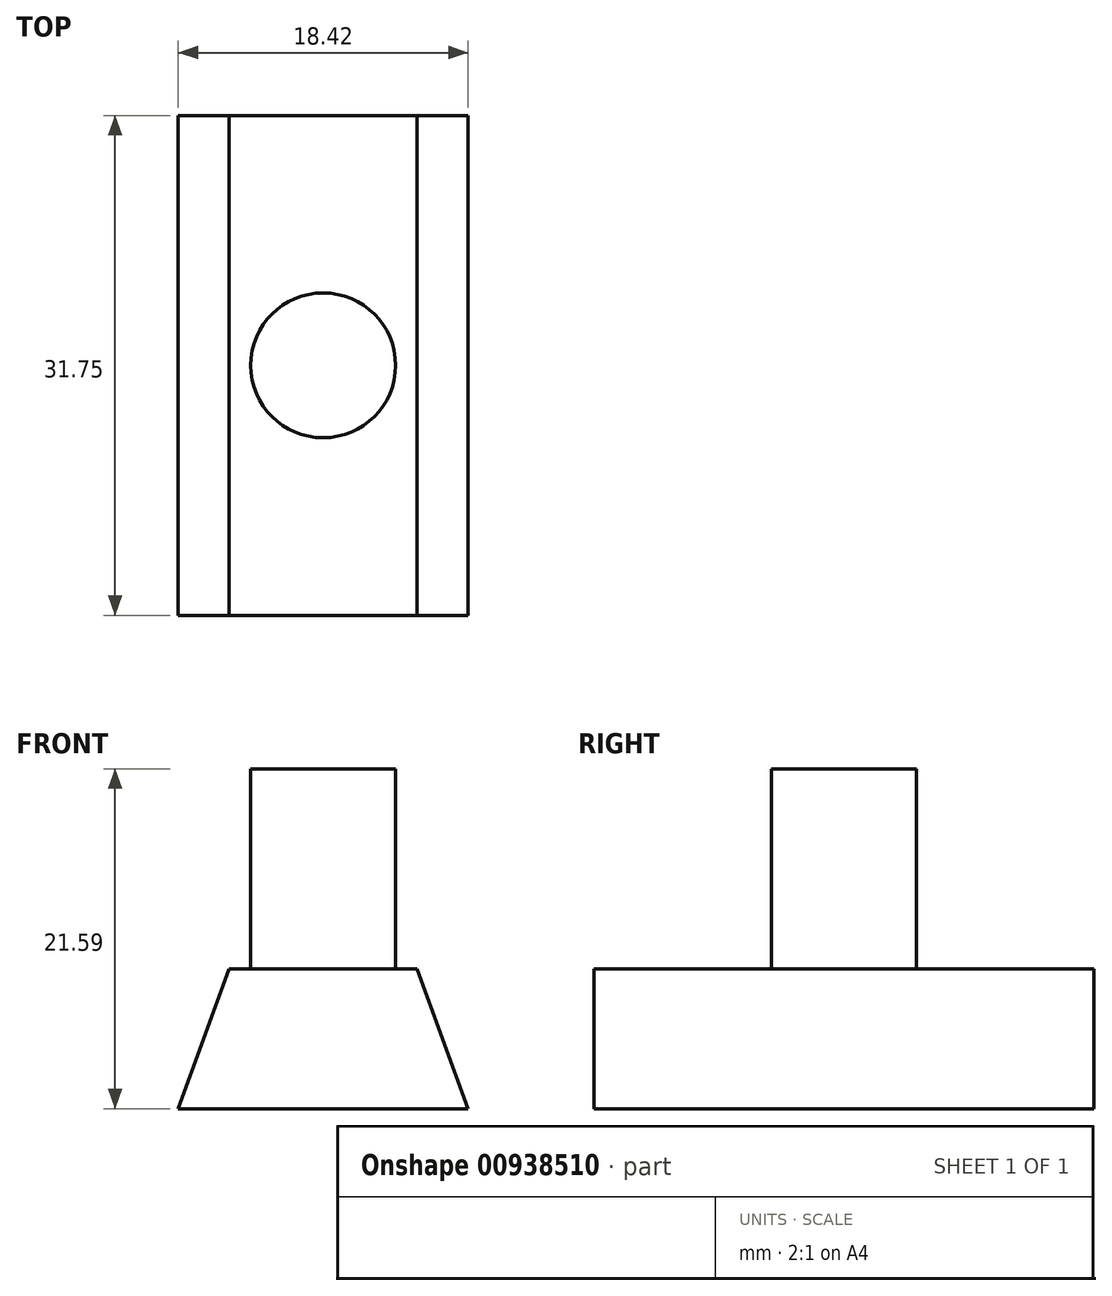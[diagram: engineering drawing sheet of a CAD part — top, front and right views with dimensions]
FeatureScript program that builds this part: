
annotation { "Feature Type Name" : "Feature", "Feature Type Description" : "" }
export const myFeature = defineFeature(function(context is Context, id is Id, definition is map)
    precondition{}
    {
        {
            var Q0;
            Q0=qCreatedBy(makeId("Front.planeOp"),FACE);
            var sketch = newSketch(context, id + "F0", { "sketchPlane" : qUnion([Q0])});
            skLineSegment(sketch, "E0", {"start": v(-9.2, 0) * mm, "end": v(9.2, 0) * mm});
            skLineSegment(sketch, "E1.MirrorCS", {"start": v(9.2, 0) * mm, "end": v(-9.2, 0) * mm});
            skLineSegment(sketch, "E2", {"start": v(-9.2, 0) * mm, "end": v(-5.97, 8.89) * mm});
            skLineSegment(sketch, "E3", {"start": v(-5.97, 8.89) * mm, "end": v(5.97, 8.89) * mm});
            skLineSegment(sketch, "E4", {"start": v(5.97, 8.89) * mm, "end": v(9.2, 0) * mm});
            skSolve(sketch);
        }
        {
            var Q0;
            Q0 = qSketchRegion(id + "F0", true);
            extrude(context, id + "F1", {"entities" : qUnion([Q0]), "oppositeDirection" : true, "depth" : 31.75 * mm, "offsetDistance" : 25 * mm});
        }
        {
            var Q0;
            Q0=makeQuery(id+"F1.opExtrude","SWEPT_FACE",FACE,{"disambiguationData":[OSD([sQuery(id+"F0.wireOp",EDGE,"E3")])]});
            var sketch = newSketch(context, id + "F2", { "sketchPlane" : qUnion([Q0])});
            skLineSegment(sketch, "E5", {"start": v(0, 31.75) * mm, "end": v(0, 15.88) * mm, "construction": true});
            skCircle(sketch, "E6", {"center": v(0, 15.88) * mm, "radius": 4.6 * mm});
            skSolve(sketch);
        }
        {
            var Q0;
            Q0 = qSketchRegion(id + "F2", true);
            extrude(context, id + "F3", {"entities" : qUnion([Q0]), "operationType" : NewBodyOperationType.ADD, "depth" : 12.7 * mm, "offsetDistance" : 25 * mm});
        }
    });
